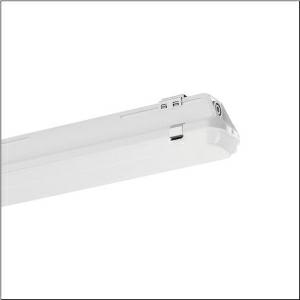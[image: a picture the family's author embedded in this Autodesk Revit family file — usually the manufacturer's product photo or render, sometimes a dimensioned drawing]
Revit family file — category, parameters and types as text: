
# Revit family: monsun_r__21_parking_51fg207l430k_4ecc
name_source: partatom
category: Lighting Fixtures
units: mm (PartAtom-declared; Revit-internal decimal feet)

## family parameters
Cut with Voids When Loaded = No
Host = Face
Light Source = No
Part Type = Normal
Room Calculation Point = No
Round Connector Dimension = Use Diameter
Shared = No

## types (1)
- Monsun® 21 parking (1 x LED, 3930 lm, 24.7 W, 4000K)
    Apparent Load = 25 VA
    CIE Flux Codes = 45 75 93 94 100
    Color Rendering = 80
    Color Temperature = 4000K
    Default Elevation = 1800 mm
    Description = Monsun® 21 parking, damp-proof luminaire, chain hanger, primary optical cover: enclosure, of PC, light emission: direct distribution, primary light characteristic: symmetric, installation type: suspended mounting, surface-mounted, horizontal mounting, vertical mounting, LED, rated luminous flux: 3.930lm, luminous efficacy: 159lm/W, light colour: 840, colour temperature: 4000K, control gear: ON/OFF, with terminal, 3-pole, max. 2.5mm², mains connection: 220..240V, AC, 50/60Hz, rated input power: 25W, housing, of glass-fibre reinforced plastic, uncoated, bright grey, incl. chain hanger, length: 1.299mm, width: 90mm, height: 88mm, clip for enclosure, of stainless steel (V2A), ceiling mounting element, of stainless steel (V2A), chain hanger, of stainless steel (V2A), protection rating (complete): IP66, insulation class (complete): insulation class I (protective earthing), certification: CE, ENEC, VDE, UKCA, protection symbol: D, impact resistance: IK08, permissible operating ambient temperature: -25..+35°C, standard: EN 50419, EN 60598-2-1, corresponds to IFS (International Featured Standards) requirements for safety and quality in the food industry, for indoor or canopied outdoor use, no direct snow, no direct sun, no direct rain, LABS conformity tested according to VDMA 24364:2018-05, contact your sales advisor before using the luminaires in applications with unclear chemical exposure, large temperature fluctuations or condensation-forming humidity, packaging unit: 1 piece
    Height = 88 mm
    Lamp = 1 x LED
    Lamp Light Flux = 3930 lm
    Lamp Power = 24.7 W
    Lamp count = 1
    Length = 1299 mm
    Luminous efficacy = 159 lm/W
    Manufacturer = Siteco
    ModVariant = No
    Model = 51FG207L430K
    Mounting Place = Ceiling
    Mounting Type = Surface mounted
    Number of Poles = 1
    OnlyDefault = Yes
    Power Factor = 1
    Product Name = Monsun® 21 parking
    Product group = damp-proof luminaire
    ProductGroupID = 300
    Protection Class = Protection class I
    Protection Degree = IP 66
    RLX_Detail_Level = 1
    RLX_Emergency_Light_Flux = 0 lm
    RLX_Emergency_Type = 0
    RLX_Emergency_Type_DB = No
    RlxData = <blob elided: 89733 chars, md5=42b72c29>
    Socket = socket
    Standby Power = 0 W
    System Light Flux = 3930 lm
    System Power = 25 W
    Type Comments = Product without accessories
    Type Image = l_1319656.jpg
    URL = http://relux.com
    VarID = ---
    Voltage = 0 V
    Weight = 0.00 kg
    Width = 90 mm

## geometry (parser evidence)
native form markers: Blend x4, Sweep x14
no freeform markers — native parametric forms only
